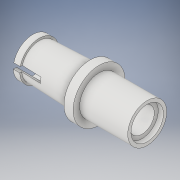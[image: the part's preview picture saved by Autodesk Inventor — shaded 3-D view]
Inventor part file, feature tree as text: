
AUTODESK INVENTOR PART (.ipt)
format: ipt  version: 2017 (Build 210142000, 142)  size: 178,688 bytes
history: native  units: in
note: dims shown in document units (in); Inventor stores cm internally (conversion verified against a paired STEP export)
features: sketch x2, revolve x1, plane x1, extrude x1
ambient origin geometry x8: Origin, YZ Plane, XZ Plane, XY Plane, X Axis, Y Axis, Z Axis, Center Point
bodies: Solid1 (feature_tree)
feature tree (5):
  revolve  "Revolution1"  [1 undecoded]
  plane  "Work Plane1"
  extrude  "Extrusion1"  Depth=0.05in
  sketch  "Sketch1"  dims[d0=0.88in d4=0.025in]
  sketch  "Sketch2"  dims[d7=0.03in d11=0.05in d15=0.33in d17=0.03in d18=0.05in d19=0.015in d21=90.0deg d22=0.04in d23=0.37in d24=0.37in d25=0.44in d26=0.63in d27=0.075in d28=0.125in d29=0.325in d30=0.5321in d31=0.0254in d32=0.0643in d33=0.0in d34=0.275in d35=0.2777in d36=0.88in d37=0.88in d38=90.0deg d44=0.2in d45=0.04in d46=0.1163in d47=0.25in d48=0.0in]
note: 1 required parameter value undecoded (feature->parameter linkage not recoverable at this tier; creation-order binding heuristic only, values carry confidence <= 0.55)
